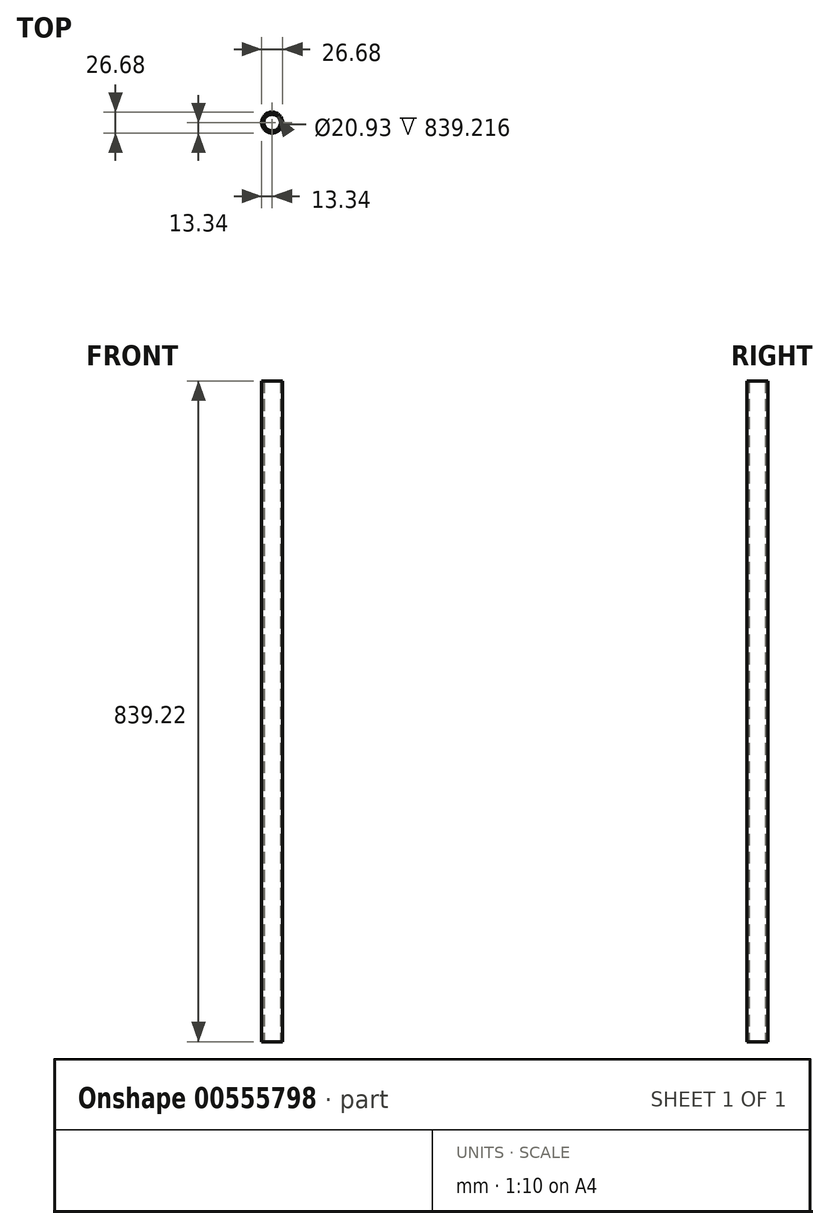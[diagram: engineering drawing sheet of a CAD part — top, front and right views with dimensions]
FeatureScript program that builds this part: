
annotation { "Feature Type Name" : "Feature", "Feature Type Description" : "" }
export const myFeature = defineFeature(function(context is Context, id is Id, definition is map)
    precondition{}
    {
        {
            var Q0;
            Q0=qCreatedBy(makeId("Top.planeOp"),FACE);
            var sketch = newSketch(context, id + "F0", { "sketchPlane" : qUnion([Q0])});
            skCircle(sketch, "E0", {"center": v(0, 0) * mm, "radius": 13.33 * mm});
            skCircle(sketch, "E1", {"center": v(0, 0) * mm, "radius": 10.46 * mm});
            skSolve(sketch);
        }
        {
            var Q0;
            Q0=qSketchRegion(id+"F0",true);
            extrude(context, id + "F1", {"entities" : qUnion([Q0]), "depth" : 839.22 * mm, "offsetDistance" : 25.4 * mm});
        }
    });
